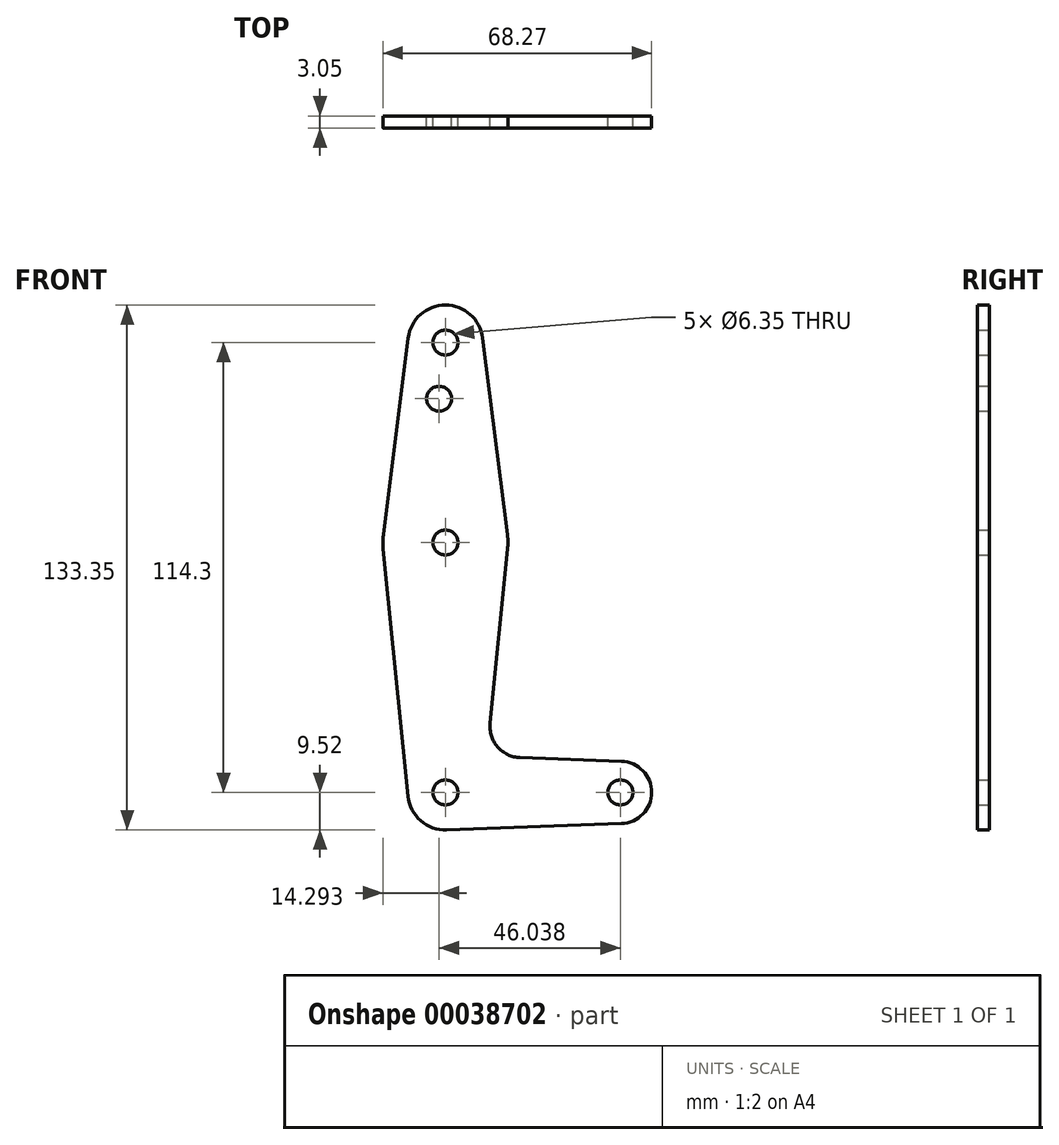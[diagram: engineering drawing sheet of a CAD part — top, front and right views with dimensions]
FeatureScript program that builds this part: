
annotation { "Feature Type Name" : "Feature", "Feature Type Description" : "" }
export const myFeature = defineFeature(function(context is Context, id is Id, definition is map)
    precondition{}
    {
        {
            var Q0;
            Q0=qCreatedBy(makeId("Front.planeOp"),FACE);
            var sketch = newSketch(context, id + "F0", { "sketchPlane" : qUnion([Q0])});
            skLineSegment(sketch, "E0", {"start": v(0, 114.3) * mm, "end": v(0, 0) * mm, "construction": true});
            skLineSegment(sketch, "E1", {"start": v(0, 0) * mm, "end": v(44.45, 0) * mm, "construction": true});
            skCircle(sketch, "E2", {"center": v(0, 114.3) * mm, "radius": 9.53 * mm});
            skCircle(sketch, "E3", {"center": v(0, 63.5) * mm, "radius": 15.88 * mm});
            skCircle(sketch, "E4", {"center": v(0, 0) * mm, "radius": 9.53 * mm});
            skCircle(sketch, "E5", {"center": v(44.45, 0) * mm, "radius": 7.94 * mm});
            skLineSegment(sketch, "E6", {"start": v(9.45, 115.5) * mm, "end": v(15.75, 65.48) * mm});
            skLineSegment(sketch, "E7", {"start": v(-9.45, 115.5) * mm, "end": v(-15.75, 65.48) * mm});
            skLineSegment(sketch, "E8", {"start": v(15.8, 61.91) * mm, "end": v(11.34, 17.6) * mm});
            skLineSegment(sketch, "E9", {"start": v(-15.8, 61.91) * mm, "end": v(-9.48, -0.95) * mm});
            skLineSegment(sketch, "E10", {"start": v(18.97, 8.85) * mm, "end": v(44.73, 7.93) * mm});
            skLineSegment(sketch, "E11", {"start": v(0.34, -9.52) * mm, "end": v(44.73, -7.93) * mm});
            skPoint(sketch, "E12.newPointA", {"position": v(9.48, -0.95) * mm});
            skArc(sketch, "E12.filletArc", {"start": v(11.34, 17.6) * mm, "mid": v(13.26, 11.57) * mm, "end": v(18.97, 8.85) * mm});
            skCircle(sketch, "E13", {"center": v(-1.59, 100.03) * mm, "radius": 3.18 * mm});
            skCircle(sketch, "E14", {"center": v(0, 114.3) * mm, "radius": 3.18 * mm});
            skCircle(sketch, "E15", {"center": v(0, 63.5) * mm, "radius": 3.18 * mm});
            skCircle(sketch, "E16", {"center": v(0, 0) * mm, "radius": 3.18 * mm});
            skCircle(sketch, "E17", {"center": v(44.45, 0) * mm, "radius": 3.18 * mm});
            skSolve(sketch);
        }
        {
            var Q0;
            Q0 = qSketchRegion(id + "F0", true);
            extrude(context, id + "F1", {"entities" : qUnion([Q0]), "depth" : 3.05 * mm});
        }
    });
